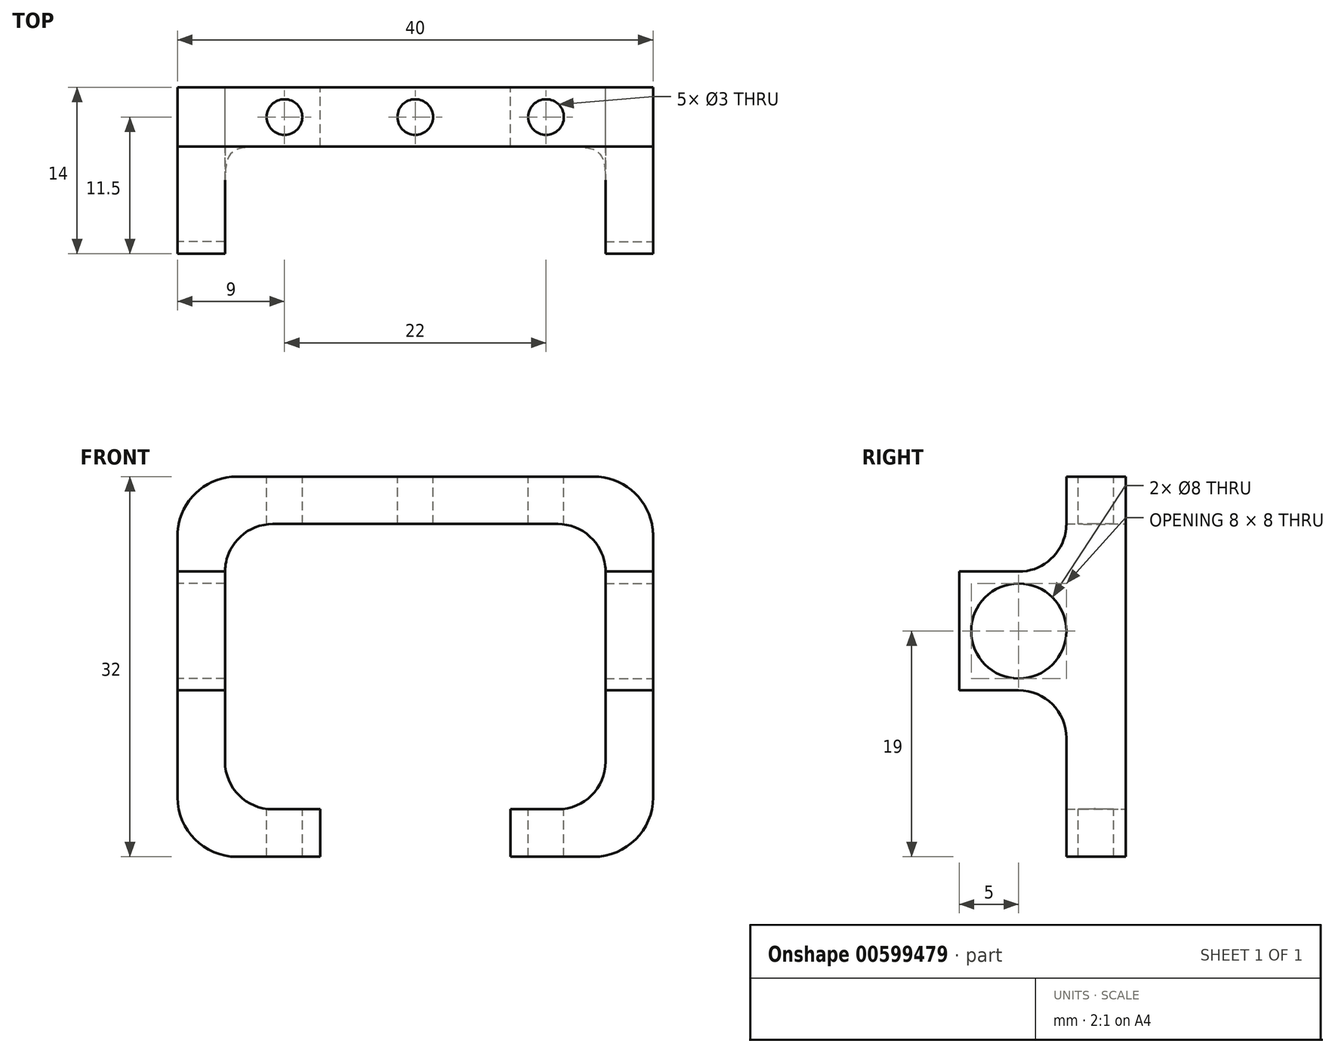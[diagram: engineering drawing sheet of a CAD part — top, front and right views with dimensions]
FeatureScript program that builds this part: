
annotation { "Feature Type Name" : "Feature", "Feature Type Description" : "" }
export const myFeature = defineFeature(function(context is Context, id is Id, definition is map)
    precondition{}
    {
        {
            var Q0;
            Q0=qCreatedBy(makeId("Front.planeOp"),FACE);
            var sketch = newSketch(context, id + "F0", { "sketchPlane" : qUnion([Q0])});
            skLineSegment(sketch, "E0.bottom", {"start": v(0, 16) * mm, "end": v(-20, 16) * mm});
            skLineSegment(sketch, "E0.top", {"start": v(-8, -16) * mm, "end": v(-20, -16) * mm});
            skLineSegment(sketch, "E0.right", {"start": v(-20, 16) * mm, "end": v(-20, -16) * mm});
            skPoint(sketch, "E0.middle", {"position": v(0, 0) * mm});
            skLineSegment(sketch, "E1.0", {"start": v(-16, 12) * mm, "end": v(-16, -12) * mm});
            skLineSegment(sketch, "E1.1", {"start": v(0, 12) * mm, "end": v(-16, 12) * mm});
            skLineSegment(sketch, "E1.3", {"start": v(-8, -12) * mm, "end": v(-16, -12) * mm});
            skLineSegment(sketch, "E2", {"start": v(0, 16) * mm, "end": v(0, 12) * mm});
            skLineSegment(sketch, "E3", {"start": v(-8, -16) * mm, "end": v(-8, -12) * mm});
            skPoint(sketch, "E4", {"position": v(-20, 0) * mm});
            skSolve(sketch);
        }
        {
            var Q0;
            Q0=makeQuery(id+"F0.imprint","IMPRINT",FACE,{"disambiguationData":[TD([[makeQuery(id+"F0.imprint","IMPRINT",EDGE,{"derivedFrom":sQuery(id+"F0.wireOp",EDGE,"E0.bottom")}),1.0]])]});
            extrude(context, id + "F1", {"entities" : qUnion([Q0]), "depth" : 14 * mm, "offsetDistance" : 25 * mm});
        }
        {
            var Q0;
            Q0=makeQuery(id+"F1.opExtrude","SWEPT_FACE",FACE,{"disambiguationData":[OSD([sQuery(id+"F0.wireOp",EDGE,"E0.right")])]});
            var sketch = newSketch(context, id + "F2", { "sketchPlane" : qUnion([Q0])});
            skCircle(sketch, "E5", {"center": v(9, 3) * mm, "radius": 4 * mm});
            skLineSegment(sketch, "E6", {"start": v(5, -16) * mm, "end": v(5, -2) * mm});
            skLineSegment(sketch, "E7", {"start": v(5, -2) * mm, "end": v(14, -2) * mm});
            skLineSegment(sketch, "E8", {"start": v(6.17, 3) * mm, "end": v(11.83, 3) * mm, "construction": true});
            skLineSegment(sketch, "E9.MirrorCS", {"start": v(5, 8) * mm, "end": v(14, 8) * mm});
            skLineSegment(sketch, "E10.MirrorCS", {"start": v(5, 22) * mm, "end": v(5, 8) * mm});
            skSolve(sketch);
        }
        {
            var Q0;
            {var subQ0=sQuery(id+"F2.wireOp",EDGE,"E9.MirrorCS");Q0=makeQuery(id+"F2.imprint","IMPRINT",FACE,{"disambiguationData":[TD([[makeQuery(id+"F2.imprint","IMPRINT",EDGE,{"derivedFrom":subQ0}),1.0]])]});}
            var Q1;
            Q1=makeQuery(id+"F2.imprint","IMPRINT",FACE,{"disambiguationData":[TD([[makeQuery(id+"F2.imprint","IMPRINT",EDGE,{"derivedFrom":sQuery(id+"F2.wireOp",EDGE,"E5")}),1.0]])]});
            var Q2;
            {var subQ0=sQuery(id+"F2.wireOp",EDGE,"E6");Q2=makeQuery(id+"F2.imprint","IMPRINT",FACE,{"disambiguationData":[TD([[makeQuery(id+"F2.imprint","IMPRINT",EDGE,{"derivedFrom":subQ0}),-1.0]])]});}
            extrude(context, id + "F3", {"entities" : qUnion([Q0, Q1, Q2]), "operationType" : NewBodyOperationType.REMOVE, "endBound" : BoundingType.THROUGH_ALL, "oppositeDirection" : true, "depth" : 25 * mm, "offsetDistance" : 25 * mm});
        }
        {
            var Q0;
            Q0=makeQuery(id+"F1.opExtrude","SWEPT_EDGE",EDGE,{"disambiguationData":[OSD([sQuery(id+"F0.wireOp",EDGE,"E1.0"),sQuery(id+"F0.wireOp",EDGE,"E1.1")])]});
            var Q1;
            Q1=makeQuery(id+"F1.opExtrude","SWEPT_EDGE",EDGE,{"disambiguationData":[OSD([sQuery(id+"F0.wireOp",EDGE,"E1.0"),sQuery(id+"F0.wireOp",EDGE,"E1.3")])]});
            fillet(context, id + "F4", {"entities" : qUnion([Q0, Q1]), "radius" : 4 * mm, "tangentPropagation" : true, "allowEdgeOverflow" : false});
        }
        {
            var Q0;
            Q0=makeQuery(id+"F1.opExtrude","SWEPT_EDGE",EDGE,{"disambiguationData":[OSD([sQuery(id+"F0.wireOp",EDGE,"E0.bottom"),sQuery(id+"F0.wireOp",EDGE,"E0.right")])]});
            var Q1;
            Q1=makeQuery(id+"F1.opExtrude","SWEPT_EDGE",EDGE,{"disambiguationData":[OSD([sQuery(id+"F0.wireOp",EDGE,"E0.top"),sQuery(id+"F0.wireOp",EDGE,"E0.right")])]});
            var Q2;
            Q2=makeQuery(id+"F3.boolean.opBoolean","COPY",EDGE,{"derivedFrom":makeQuery(id+"F3.opExtrude","SWEPT_EDGE",EDGE,{"disambiguationData":[OSD([sQuery(id+"F0.wireOp",EDGE,"E0.right"),sQuery(id+"F2.wireOp",EDGE,"E9.MirrorCS")])]})});
            var Q3;
            Q3=makeQuery(id+"F3.boolean.opBoolean","COPY",EDGE,{"derivedFrom":makeQuery(id+"F3.opExtrude","SWEPT_EDGE",EDGE,{"disambiguationData":[OSD([sQuery(id+"F0.wireOp",EDGE,"E0.right"),sQuery(id+"F2.wireOp",EDGE,"E7")])]})});
            fillet(context, id + "F5", {"entities" : qUnion([Q0, Q1, Q2, Q3]), "radius" : 5 * mm, "tangentPropagation" : true, "allowEdgeOverflow" : false});
        }
        {
            var Q0;
            Q0=makeQuery(id+"F3.boolean.opBoolean","COPY",EDGE,{"derivedFrom":makeQuery(id+"F3.opExtrude","SWEPT_EDGE",EDGE,{"disambiguationData":[OSD([sQuery(id+"F2.wireOp",EDGE,"E9.MirrorCS"),sQuery(id+"F2.wireOp",EDGE,"E10.MirrorCS")])]})});
            var Q1;
            Q1=makeQuery(id+"F3.boolean.opBoolean","COPY",EDGE,{"derivedFrom":makeQuery(id+"F3.opExtrude","SWEPT_EDGE",EDGE,{"disambiguationData":[OSD([sQuery(id+"F2.wireOp",EDGE,"E6"),sQuery(id+"F2.wireOp",EDGE,"E7")])]})});
            fillet(context, id + "F6", {"entities" : qUnion([Q0, Q1]), "radius" : 4 * mm, "tangentPropagation" : true, "allowEdgeOverflow" : false});
        }
        {
            var Q0;
            Q0=makeQuery(id+"F1.opExtrude","SWEPT_FACE",FACE,{"disambiguationData":[OSD([sQuery(id+"F0.wireOp",EDGE,"E0.bottom")])]});
            var sketch = newSketch(context, id + "F7", { "sketchPlane" : qUnion([Q0])});
            skPoint(sketch, "E11", {"position": v(0, -2.5) * mm});
            skPoint(sketch, "E12.MirrorP", {"position": v(-11, -2.5) * mm});
            skSolve(sketch);
        }
        {
            var Q0;
            Q0=sQuery(id+"F7.wireOp",VERTEX,"f9a117d3-01f1-4563-8390-42ee49890b19");
            var Q1;
            Q1=sQuery(id+"F7.wireOp",VERTEX,"E12.MirrorP");
            var Q2;
            Q2=sQuery(id+"F7.wireOp",VERTEX,"E11");
            var Q3;
            Q3=makeQuery(id+"F1.opExtrude","SWEPT_BODY",BODY,{"disambiguationData":[OSD([sQuery(id+"F0.wireOp",EDGE,"E0.bottom"),sQuery(id+"F0.wireOp",EDGE,"E0.top"),sQuery(id+"F0.wireOp",EDGE,"E0.left"),sQuery(id+"F0.wireOp",EDGE,"E0.right"),sQuery(id+"F0.wireOp",EDGE,"E1.0"),sQuery(id+"F0.wireOp",EDGE,"E1.1"),sQuery(id+"F0.wireOp",EDGE,"E1.2"),sQuery(id+"F0.wireOp",EDGE,"E1.3")])]});
            hole(context, id + "F8", {"style" : HoleStyle.SIMPLE, "endStyle" : HoleEndStyle.THROUGH, "holeDiameter" : 3 * mm, "majorDiameter" : 5 * mm, "isTappedThrough" : true, "tappedDepth" : 12 * mm, "tapClearance" : 3, "locations" : qUnion([Q0, Q1, Q2]), "scope" : qUnion([Q3])});
        }
        {
            var Q0;
            Q0=makeQuery(id+"F1.opExtrude","SWEPT_BODY",BODY,{"disambiguationData":[OSD([sQuery(id+"F0.wireOp",EDGE,"E0.bottom"),sQuery(id+"F0.wireOp",EDGE,"E0.top"),sQuery(id+"F0.wireOp",EDGE,"E0.right"),sQuery(id+"F0.wireOp",EDGE,"E1.0"),sQuery(id+"F0.wireOp",EDGE,"E1.1"),sQuery(id+"F0.wireOp",EDGE,"E1.3"),sQuery(id+"F0.wireOp",EDGE,"E2"),sQuery(id+"F0.wireOp",EDGE,"E3")])]});
            var Q1;
            Q1=qCreatedBy(makeId("Right.planeOp"),FACE);
            mirror(context, id + "F9", {"operationType" : NewBodyOperationType.ADD, "entities" : qUnion([Q0]), "mirrorPlane" : qUnion([Q1])});
        }
    });
